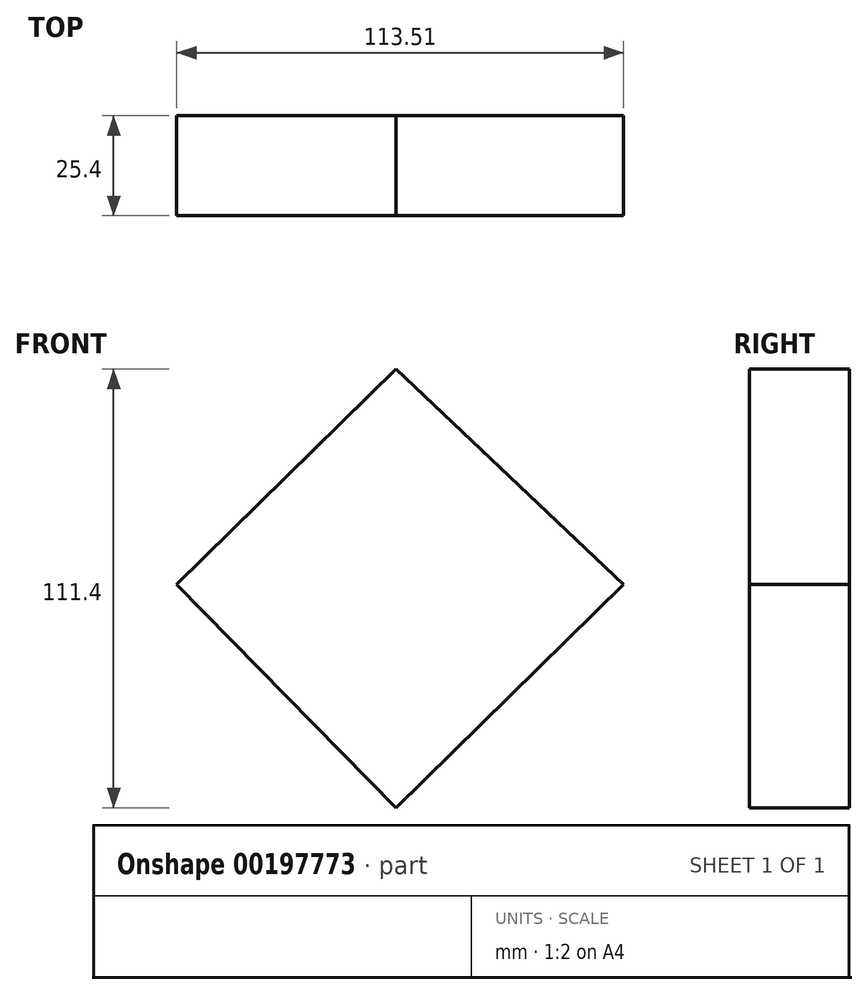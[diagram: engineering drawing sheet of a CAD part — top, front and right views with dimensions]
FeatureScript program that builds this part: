
annotation { "Feature Type Name" : "Feature", "Feature Type Description" : "" }
export const myFeature = defineFeature(function(context is Context, id is Id, definition is map)
    precondition{}
    {
        {
            var Q0;
            Q0=qCreatedBy(makeId("Front.planeOp"),FACE);
            var sketch = newSketch(context, id + "F0", { "sketchPlane" : qUnion([Q0])});
            skLineSegment(sketch, "E0", {"start": v(-55.69, 0) * mm, "end": v(0, -56.75) * mm});
            skLineSegment(sketch, "E1", {"start": v(0, -56.75) * mm, "end": v(57.82, 0) * mm});
            skLineSegment(sketch, "E2", {"start": v(-55.69, 0) * mm, "end": v(0, 54.65) * mm});
            skLineSegment(sketch, "E3", {"start": v(0, 54.65) * mm, "end": v(57.82, 0) * mm});
            skSolve(sketch);
        }
        {
            var Q0;
            Q0=makeQuery(id+"F0.imprint","IMPRINT",FACE,{"disambiguationData":[TD([[makeQuery(id+"F0.imprint","IMPRINT",EDGE,{"derivedFrom":sQuery(id+"F0.wireOp",EDGE,"E0")}),1.0]])]});
            extrude(context, id + "F1", {"entities" : qUnion([Q0]), "depth" : 25.4 * mm});
        }
    });
